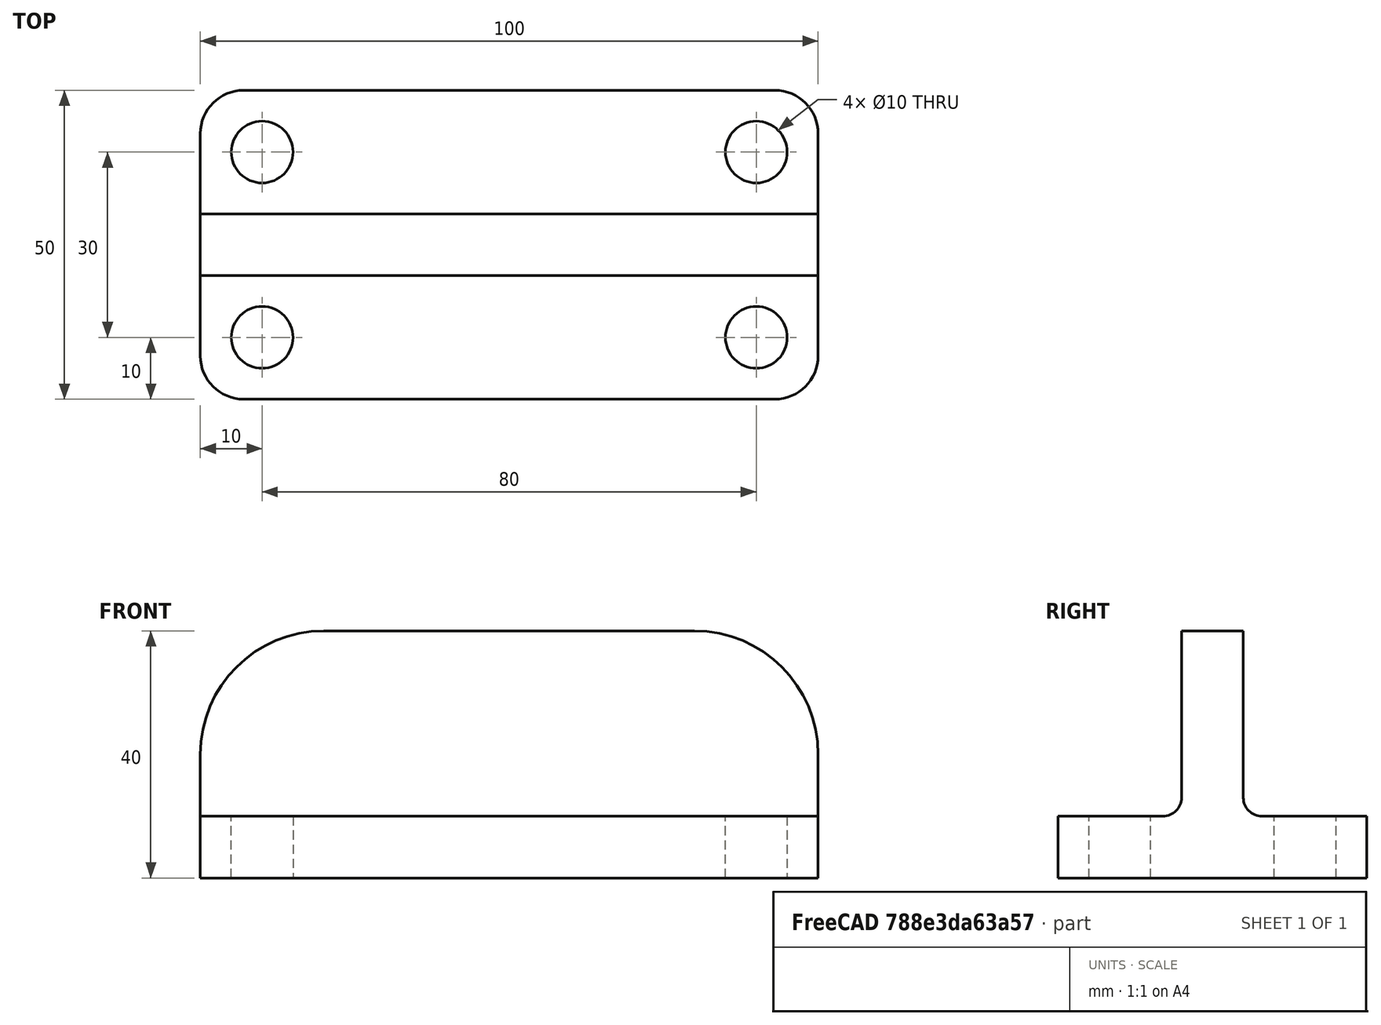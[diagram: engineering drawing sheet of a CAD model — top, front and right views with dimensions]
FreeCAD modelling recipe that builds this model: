
FCSTD DOCUMENT  (FreeCAD 0.21R33771 (Git))
Label: item_01
License: All rights reserved
LicenseURL: http://en.wikipedia.org/wiki/All_rights_reserved
objects: TechDraw::DrawViewDimension×10, Sketcher::SketchObject×3, PartDesign::Fillet×3, TechDraw::DrawProjGroupItem×3, PartDesign::Pad×2, TechDraw::DrawSVGTemplate×2, TechDraw::DrawPage×2, PartDesign::Pocket×1, PartDesign::Body×1, TechDraw::DrawViewPart×1, TechDraw::DrawProjGroup×1
note: 32 computed .brp shape members not serialized (recipe doc carries the construction recipe); baked Part::Feature solids carry a one-line shape summary decoded from their .brp

FEATURE [Sketcher::SketchObject] Sketch
  FullyConstrained = true
  MapMode = 5
  Support = -> [XY_Plane]
  sketch-geometry (4):
    g0: LineSegment StartX=0 StartY=0 StartZ=0 EndX=100 EndY=0 EndZ=0
    g1: LineSegment StartX=100 StartY=0 StartZ=0 EndX=100 EndY=50 EndZ=0
    g2: LineSegment StartX=100 StartY=50 StartZ=0 EndX=0 EndY=50 EndZ=0
    g3: LineSegment StartX=0 StartY=50 StartZ=0 EndX=0 EndY=0 EndZ=0
  constraints (11):
    c: Coincident(g0,g1)
    c: Coincident(g1,g2)
    c: Coincident(g2,g3)
    c: Coincident(g3,g0)
    c: Horizontal(g0)
    c: Horizontal(g2)
    c: Vertical(g1)
    c: Vertical(g3)
    c: Coincident(g0,g-1)
    c: DistanceX(g2,g2) = 100
    c: DistanceY(g3,g3) = 50
FEATURE [PartDesign::Pad] Pad
  Direction = (0,0,1)
  Length = 10
  Length2 = 10
  Profile = -> Sketch
  ReferenceAxis = -> Sketch [N_Axis]
  Type = 0
FEATURE [Sketcher::SketchObject] Sketch001
  ExternalGeometry = -> [Pad]
  FullyConstrained = true
  MapMode = 5
  Placement = pos=(0,0,10) rot=(0,0,1;0rad)
  Support = -> [Pad]
  sketch-geometry (4):
    g0: LineSegment StartX=0 StartY=30 StartZ=0 EndX=100 EndY=30 EndZ=0
    g1: LineSegment StartX=100 StartY=30 StartZ=0 EndX=100 EndY=20 EndZ=0
    g2: LineSegment StartX=100 StartY=20 StartZ=0 EndX=0 EndY=20 EndZ=0
    g3: LineSegment StartX=0 StartY=20 StartZ=0 EndX=0 EndY=30 EndZ=0
  constraints (12):
    c: Coincident(g0,g1)
    c: Coincident(g1,g2)
    c: Coincident(g2,g3)
    c: Coincident(g3,g0)
    c: Horizontal(g0)
    c: Horizontal(g2)
    c: Vertical(g1)
    c: Vertical(g3)
    c: DistanceY(g3,g3) = 10
    c: DistanceY(g-3,g2) = 20
    c: PointOnObject(g2,g-3)
    c: PointOnObject(g0,g-4)
FEATURE [PartDesign::Pad] Pad001
  BaseFeature = -> Pad
  Direction = (0,0,1)
  Length = 30
  Length2 = 10
  Profile = -> Sketch001
  ReferenceAxis = -> Sketch001 [N_Axis]
  Type = 0
FEATURE [Sketcher::SketchObject] Sketch002
  ExternalGeometry = -> [Pad001]
  FullyConstrained = true
  MapMode = 5
  Placement = pos=(0,0,10) rot=(0,0,1;0rad)
  Support = -> [Pad001]
  sketch-geometry (4):
    g0: Circle CenterX=10 CenterY=40 CenterZ=0 NormalX=0 NormalY=0 NormalZ=1 AngleXU=0 Radius=5
    g1: Circle CenterX=90 CenterY=40 CenterZ=0 NormalX=0 NormalY=0 NormalZ=1 AngleXU=0 Radius=5
    g2: Circle CenterX=10 CenterY=10 CenterZ=0 NormalX=0 NormalY=0 NormalZ=1 AngleXU=0 Radius=5
    g3: Circle CenterX=90 CenterY=10 CenterZ=0 NormalX=0 NormalY=0 NormalZ=1 AngleXU=0 Radius=5
  constraints (12):
    c: Radius(g0) = 5
    c: DistanceY(g0,g-3) = 10
    c: DistanceX(g-3,g0) = 10
    c: Equal(g0,g1)
    c: Equal(g1,g3)
    c: Equal(g3,g2)
    c: Horizontal(g0,g1)
    c: Horizontal(g2,g3)
    c: Vertical(g0,g2)
    c: Vertical(g3,g1)
    c: DistanceX(g3,g-3) = 10
    c: DistanceY(g-1,g3) = 10
FEATURE [PartDesign::Pocket] Pocket
  BaseFeature = -> Pad001
  Direction = (0,0,-1)
  Length = 5
  Length2 = 5
  Profile = -> Sketch002
  ReferenceAxis = -> Sketch002 [N_Axis]
  Type = 1
FEATURE [PartDesign::Fillet] Fillet
  Base = -> Pocket [Edge32,Edge29]
  BaseFeature = -> Pocket
  Radius = 20
  SupportTransform = false
  UseAllEdges = false
FEATURE [PartDesign::Fillet] Fillet001
  Base = -> Fillet [Edge31,Edge28,Edge13,Edge12]
  BaseFeature = -> Fillet
  Radius = 7
  SupportTransform = false
  UseAllEdges = false
FEATURE [PartDesign::Fillet] Fillet002
  Base = -> Fillet001 [Edge28,Edge22]
  BaseFeature = -> Fillet001
  Radius = 3
  SupportTransform = false
  UseAllEdges = false
FEATURE [PartDesign::Body] Body
  Group = -> [Sketch,Pad,Sketch001,Pad001,Sketch002,Pocket,Fillet,Fillet001,Fillet002]
  Origin = -> Origin
  Tip = -> Fillet002
FEATURE [TechDraw::DrawSVGTemplate] Template
  EditableTexts = Designed_by_Name=Reza Heshmati; Drawing_number=#4; FC-Date=Date; FC-SC=Scale; FC-SH=Sheet; FC-Title=Item_01; Subtitle=This part is for my training; Weight=Weight
  Height = 210
  Orientation = 1
  Template = <path>
  Width = 297
FEATURE [TechDraw::DrawViewPart] View
  Caption = 3D View
  CoarseView = false
  Direction = (0.57735,-0.57735,0.57735)
  Focus = 100
  HardHidden = false
  IsoCount = 0
  IsoHidden = false
  IsoVisible = false
  LockPosition = false
  Perspective = false
  Rotation = 0
  Scale = 0.8
  ScaleType = 2
  ScrubCount = 0
  SeamHidden = false
  SeamVisible = false
  SmoothHidden = false
  SmoothVisible = true
  Source = -> [Body]
  X = 239.708
  XDirection = (0.707107,0.707107,0)
  Y = 134.917
FEATURE [TechDraw::DrawProjGroupItem] ProjItem  label="Top"
  Caption = Top view
  CoarseView = false
  Direction = (4e-16,0,1)
  Focus = 100
  HardHidden = false
  IsoCount = 0
  IsoHidden = false
  IsoVisible = false
  LockPosition = true
  Perspective = false
  Rotation = 0
  RotationVector = (1,0,0)
  ScaleType = 2
  ScrubCount = 0
  SeamHidden = false
  SeamVisible = false
  SmoothHidden = false
  SmoothVisible = true
  Source = -> [Body]
  Type = 0
  X = 0
  XDirection = (1,0,-4e-16)
  Y = 0
FEATURE [TechDraw::DrawProjGroupItem] ProjItem001  label="Front"
  Caption = Front view
  CoarseView = false
  Direction = (1,0,-3e-16)
  Focus = 100
  HardHidden = false
  IsoCount = 0
  IsoHidden = false
  IsoVisible = false
  LockPosition = false
  Perspective = false
  Rotation = -90
  RotationVector = (1,0,0)
  ScaleType = 2
  ScrubCount = 0
  SeamHidden = false
  SeamVisible = false
  SmoothHidden = false
  SmoothVisible = true
  Source = -> [Body]
  Type = 2
  X = -85
  XDirection = (-3e-16,0,-1)
  Y = 0
FEATURE [TechDraw::DrawProjGroupItem] ProjItem002  label="Right"
  Caption = Side view
  CoarseView = false
  Direction = (0,-1,0)
  Focus = 100
  HardHidden = false
  IsoCount = 0
  IsoHidden = false
  IsoVisible = false
  LockPosition = false
  Perspective = false
  Rotation = 0
  RotationVector = (1,0,0)
  ScaleType = 2
  ScrubCount = 0
  SeamHidden = false
  SeamVisible = false
  SmoothHidden = false
  SmoothVisible = true
  Source = -> [Body]
  Type = 5
  X = 0
  XDirection = (1,0,-4e-16)
  Y = 70
FEATURE [TechDraw::DrawProjGroup] ProjGroup
  Anchor = -> ProjItem
  AutoDistribute = true
  LockPosition = false
  ProjectionType = 0
  Rotation = 0
  ScaleType = 0
  Source = -> [Body]
  Views = -> [ProjItem,ProjItem001,ProjItem002]
  X = 133.743
  Y = 97.2707
  spacingX = 10
  spacingY = 25
FEATURE [TechDraw::DrawViewDimension] Dimension001
  AngleOverride = false
  Arbitrary = false
  ArbitraryTolerances = false
  EqualTolerance = true
  ExtensionAngle = 0
  FormatSpec = %.2w
  FormatSpecOverTolerance = %+.2w
  FormatSpecUnderTolerance = %+.2w
  Inverted = false
  LineAngle = 0
  LockPosition = false
  MeasureType = 1
  OverTolerance = 0
  References2D = -> [ProjItem]
  Rotation = 0
  ScaleType = 0
  TheoreticalExact = false
  Type = 1
  UnderTolerance = 0
  X = -28.2054
  Y = 37.2123
FEATURE [TechDraw::DrawViewDimension] Dimension002
  AngleOverride = false
  Arbitrary = false
  ArbitraryTolerances = false
  EqualTolerance = true
  ExtensionAngle = 0
  FormatSpec = %.2w
  FormatSpecOverTolerance = %+.2w
  FormatSpecUnderTolerance = %+.2w
  Inverted = false
  LineAngle = 0
  LockPosition = false
  MeasureType = 1
  OverTolerance = 0
  References2D = -> [ProjItem]
  Rotation = 0
  ScaleType = 0
  TheoreticalExact = false
  Type = 2
  UnderTolerance = 0
  X = -57.0896
  Y = 4.57954
FEATURE [TechDraw::DrawViewDimension] Dimension003
  AngleOverride = false
  Arbitrary = false
  ArbitraryTolerances = false
  EqualTolerance = true
  ExtensionAngle = 0
  FormatSpec = %.2w
  FormatSpecOverTolerance = %+.2w
  FormatSpecUnderTolerance = %+.2w
  Inverted = false
  LineAngle = 0
  LockPosition = false
  MeasureType = 1
  OverTolerance = 0
  References2D = -> [ProjItem]
  Rotation = 0
  ScaleType = 0
  TheoreticalExact = false
  Type = 2
  UnderTolerance = 0
  X = 55.8104
  Y = 6.78425
FEATURE [TechDraw::DrawViewDimension] Dimension
  AngleOverride = false
  Arbitrary = false
  ArbitraryTolerances = false
  EqualTolerance = true
  ExtensionAngle = 0
  FormatSpec = ⌀%.2w
  FormatSpecOverTolerance = %+.2w
  FormatSpecUnderTolerance = %+.2w
  Inverted = false
  LineAngle = 0
  LockPosition = false
  MeasureType = 1
  OverTolerance = 0
  References2D = -> [ProjItem]
  Rotation = 0
  ScaleType = 0
  TheoreticalExact = false
  Type = 5
  UnderTolerance = 0
  X = -25.6421
  Y = 21.7782
FEATURE [TechDraw::DrawViewDimension] Dimension006
  AngleOverride = false
  Arbitrary = false
  ArbitraryTolerances = false
  EqualTolerance = true
  ExtensionAngle = 0
  FormatSpec = R%.2w
  FormatSpecOverTolerance = %+.2w
  FormatSpecUnderTolerance = %+.2w
  Inverted = false
  LineAngle = 0
  LockPosition = false
  MeasureType = 1
  OverTolerance = 0
  References2D = -> [ProjItem001]
  Rotation = 0
  ScaleType = 0
  TheoreticalExact = false
  Type = 4
  UnderTolerance = 0
  X = 12.2033
  Y = 2.38761
FEATURE [TechDraw::DrawViewDimension] Dimension007
  AngleOverride = false
  Arbitrary = false
  ArbitraryTolerances = false
  EqualTolerance = true
  ExtensionAngle = 0
  FormatSpec = %.2w
  FormatSpecOverTolerance = %+.2w
  FormatSpecUnderTolerance = %+.2w
  Inverted = false
  LineAngle = 0
  LockPosition = false
  MeasureType = 1
  OverTolerance = 0
  References2D = -> [ProjItem001]
  Rotation = 0
  ScaleType = 0
  TheoreticalExact = false
  Type = 2
  UnderTolerance = 0
  X = -30.8364
  Y = -10.643
FEATURE [TechDraw::DrawViewDimension] Dimension008
  AngleOverride = false
  Arbitrary = false
  ArbitraryTolerances = false
  EqualTolerance = true
  ExtensionAngle = 0
  FormatSpec = R%.2w
  FormatSpecOverTolerance = %+.2w
  FormatSpecUnderTolerance = %+.2w
  Inverted = false
  LineAngle = 0
  LockPosition = false
  MeasureType = 1
  OverTolerance = 0
  References2D = -> [ProjItem002]
  Rotation = 0
  ScaleType = 0
  TheoreticalExact = false
  Type = 4
  UnderTolerance = 0
  X = -29.7125
  Y = 12.2033
FEATURE [TechDraw::DrawViewDimension] Dimension009
  AngleOverride = false
  Arbitrary = false
  ArbitraryTolerances = false
  EqualTolerance = true
  ExtensionAngle = 0
  FormatSpec = %.2w
  FormatSpecOverTolerance = %+.2w
  FormatSpecUnderTolerance = %+.2w
  Inverted = false
  LineAngle = 0
  LockPosition = false
  MeasureType = 1
  OverTolerance = 0
  References2D = -> [ProjItem002]
  Rotation = 0
  ScaleType = 0
  TheoreticalExact = false
  Type = 2
  UnderTolerance = 0
  X = -60.2431
  Y = 7.8058
FEATURE [TechDraw::DrawViewDimension] Dimension010
  AngleOverride = false
  Arbitrary = false
  ArbitraryTolerances = false
  EqualTolerance = true
  ExtensionAngle = 0
  FormatSpec = %.2w
  FormatSpecOverTolerance = %+.2w
  FormatSpecUnderTolerance = %+.2w
  Inverted = false
  LineAngle = 0
  LockPosition = false
  MeasureType = 1
  OverTolerance = 0
  References2D = -> [ProjItem]
  Rotation = 0
  ScaleType = 0
  TheoreticalExact = false
  Type = 1
  UnderTolerance = 0
  X = 45.3313
  Y = 42.1428
FEATURE [TechDraw::DrawViewDimension] Dimension011
  AngleOverride = false
  Arbitrary = false
  ArbitraryTolerances = false
  EqualTolerance = true
  ExtensionAngle = 0
  FormatSpec = %.2w
  FormatSpecOverTolerance = %+.2w
  FormatSpecUnderTolerance = %+.2w
  Inverted = false
  LineAngle = 0
  LockPosition = false
  MeasureType = 1
  OverTolerance = 0
  References2D = -> [ProjItem]
  Rotation = 0
  ScaleType = 0
  TheoreticalExact = false
  Type = 2
  UnderTolerance = 0
  X = 55.1997
  Y = 22.003
FEATURE [TechDraw::DrawPage] Page
  KeepUpdated = true
  NextBalloonIndex = 1
  ProjectionType = 0
  Template = -> Template
  Views = -> [View,ProjGroup,Dimension,Dimension001,Dimension002,Dimension003,Dimension006,Dimension007,Dimension008,Dimension009,Dimension010,Dimension011]
FEATURE [TechDraw::DrawSVGTemplate] Template001
  EditableTexts = Designed_by_Name=Designed by Name; Drawing_number=Drawing number; FC-Date=Date; FC-SC=Scale; FC-SH=Sheet; FC-Title=Title; Subtitle=Subtitle; Weight=Weight
  Height = 210
  Orientation = 1
  Template = <path>
  Width = 297
FEATURE [TechDraw::DrawPage] Page001
  KeepUpdated = true
  NextBalloonIndex = 1
  ProjectionType = 0
  Template = -> Template001
note: 2 file-system paths scrubbed to <path> (originals preserved in the JSON sidecar)
